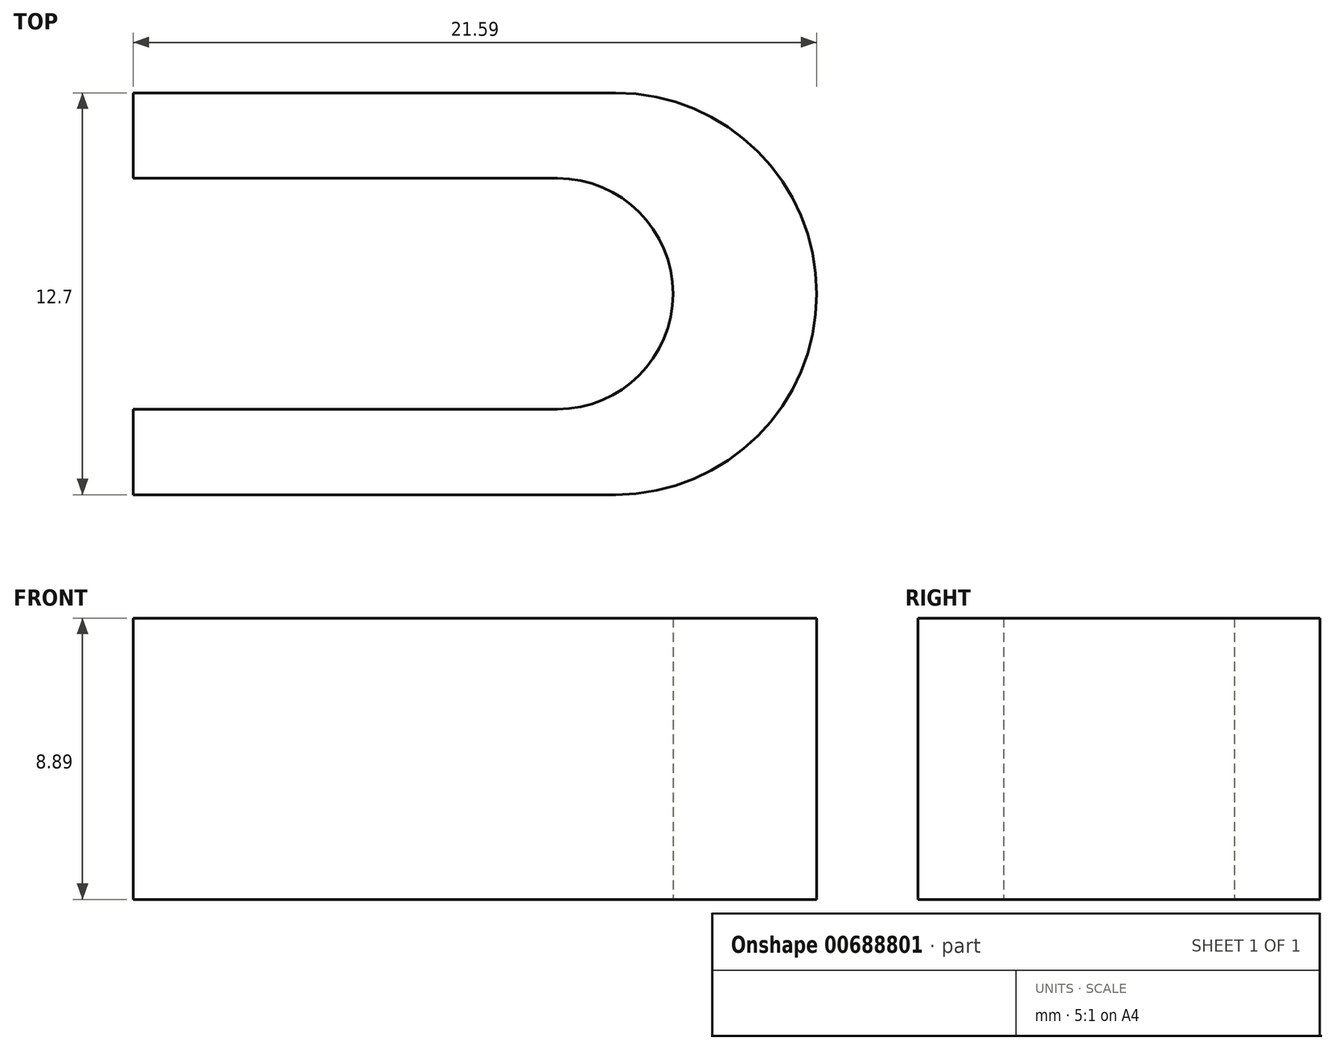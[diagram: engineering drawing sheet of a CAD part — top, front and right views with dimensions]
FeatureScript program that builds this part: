
annotation { "Feature Type Name" : "Feature", "Feature Type Description" : "" }
export const myFeature = defineFeature(function(context is Context, id is Id, definition is map)
    precondition{}
    {
        {
            var Q0;
            Q0=qCreatedBy(makeId("Top.planeOp"),FACE);
            var sketch = newSketch(context, id + "F0", { "sketchPlane" : qUnion([Q0])});
            skLineSegment(sketch, "E0.bottom", {"start": v(8.54, 6.35) * mm, "end": v(-6.7, 6.35) * mm});
            skLineSegment(sketch, "E0.top", {"start": v(8.54, -6.35) * mm, "end": v(-6.7, -6.35) * mm});
            skPoint(sketch, "E0.middle", {"position": v(0, 0) * mm});
            skLineSegment(sketch, "E1.bottom", {"start": v(6.7, 3.65) * mm, "end": v(-6.7, 3.65) * mm});
            skLineSegment(sketch, "E1.top", {"start": v(6.7, -3.65) * mm, "end": v(-6.7, -3.65) * mm});
            skArc(sketch, "E2", {"start": v(8.54, -6.35) * mm, "mid": v(14.9, 0) * mm, "end": v(8.54, 6.35) * mm});
            skArc(sketch, "E3", {"start": v(6.7, -3.65) * mm, "mid": v(10.35, 0) * mm, "end": v(6.7, 3.65) * mm});
            skLineSegment(sketch, "E4", {"start": v(-6.7, 3.65) * mm, "end": v(-6.7, 6.35) * mm});
            skLineSegment(sketch, "E5", {"start": v(-6.7, 6.35) * mm, "end": v(-6.7, 3.65) * mm});
            skLineSegment(sketch, "E6", {"start": v(-6.7, -6.35) * mm, "end": v(-6.7, -3.65) * mm});
            skPoint(sketch, "E7.orphan", {"position": v(-8.54, 6.35) * mm});
            skPoint(sketch, "E8.orphan", {"position": v(-8.54, -6.35) * mm});
            skSolve(sketch);
        }
        {
            var Q0;
            Q0=makeQuery(id+"F0.imprint","IMPRINT",FACE,{"disambiguationData":[TD([[makeQuery(id+"F0.imprint","IMPRINT",EDGE,{"derivedFrom":sQuery(id+"F0.wireOp",EDGE,"E0.bottom")}),1.0]])]});
            extrude(context, id + "F1", {"entities" : qUnion([Q0]), "depth" : 8.9 * mm, "offsetDistance" : 25.4 * mm});
        }
    });
